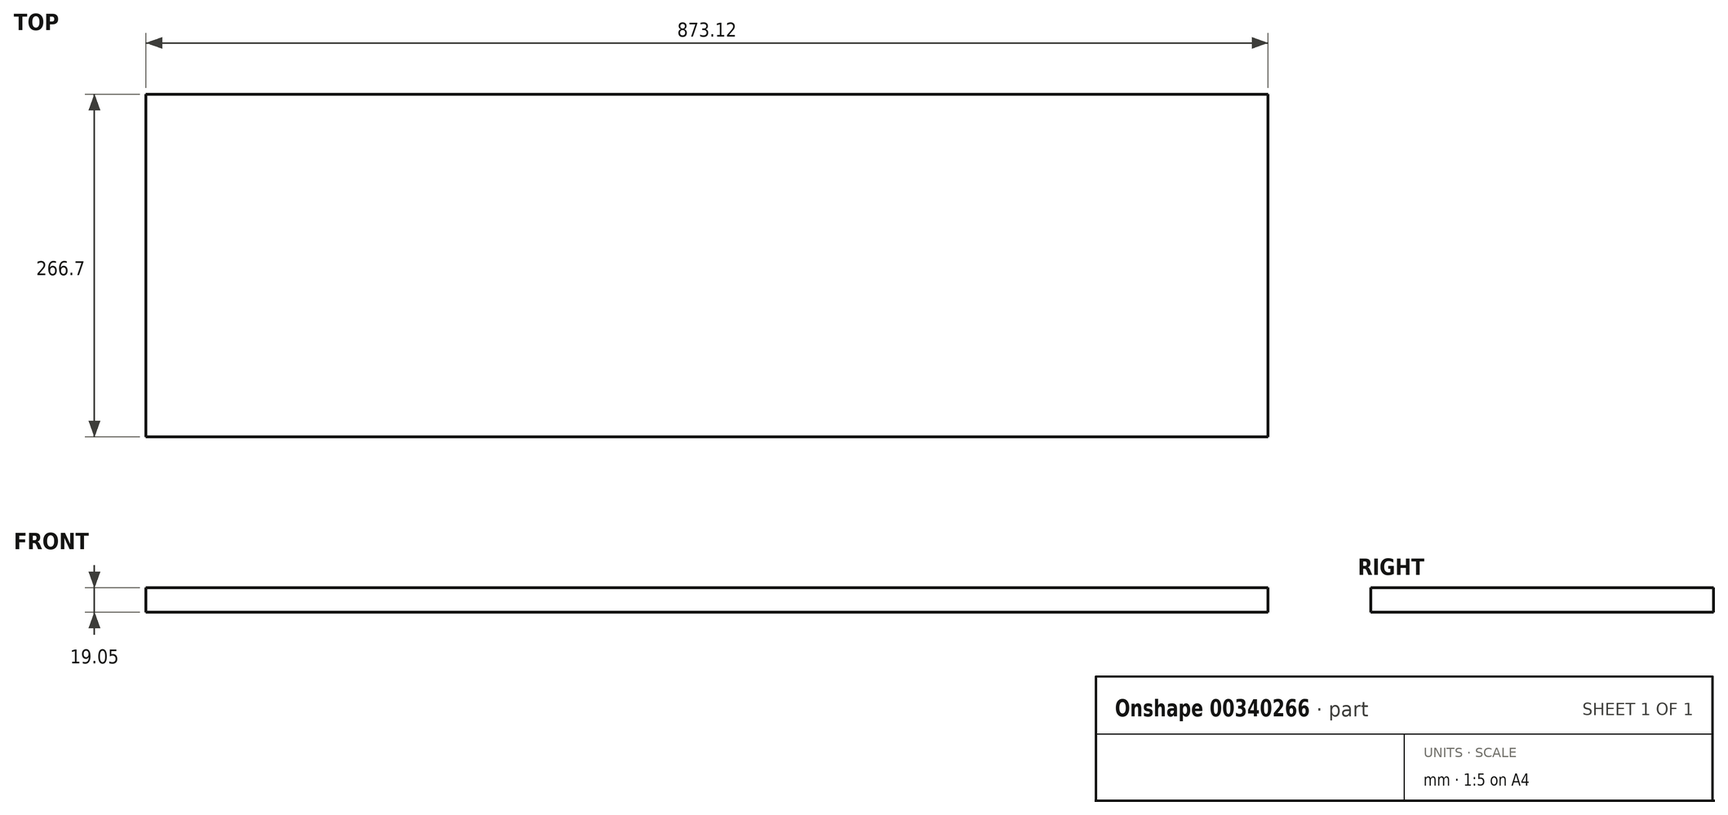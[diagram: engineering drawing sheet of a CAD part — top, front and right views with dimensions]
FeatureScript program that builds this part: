
annotation { "Feature Type Name" : "Feature", "Feature Type Description" : "" }
export const myFeature = defineFeature(function(context is Context, id is Id, definition is map)
    precondition{}
    {
        {
            var Q0;
            Q0=qCreatedBy(makeId("Top.planeOp"),FACE);
            var sketch = newSketch(context, id + "F0", { "sketchPlane" : qUnion([Q0])});
            skLineSegment(sketch, "E0.bottom", {"start": v(436.56, -133.35) * mm, "end": v(-436.56, -133.35) * mm});
            skLineSegment(sketch, "E0.top", {"start": v(436.56, 133.35) * mm, "end": v(-436.56, 133.35) * mm});
            skLineSegment(sketch, "E0.left", {"start": v(436.56, -133.35) * mm, "end": v(436.56, 133.35) * mm});
            skLineSegment(sketch, "E0.right", {"start": v(-436.56, -133.35) * mm, "end": v(-436.56, 133.35) * mm});
            skPoint(sketch, "E0.middle", {"position": v(0, 0) * mm});
            skSolve(sketch);
        }
        {
            var Q0;
            Q0 = qSketchRegion(id + "F0", true);
            extrude(context, id + "F1", {"entities" : qUnion([Q0]), "depth" : 19.05 * mm});
        }
    });
